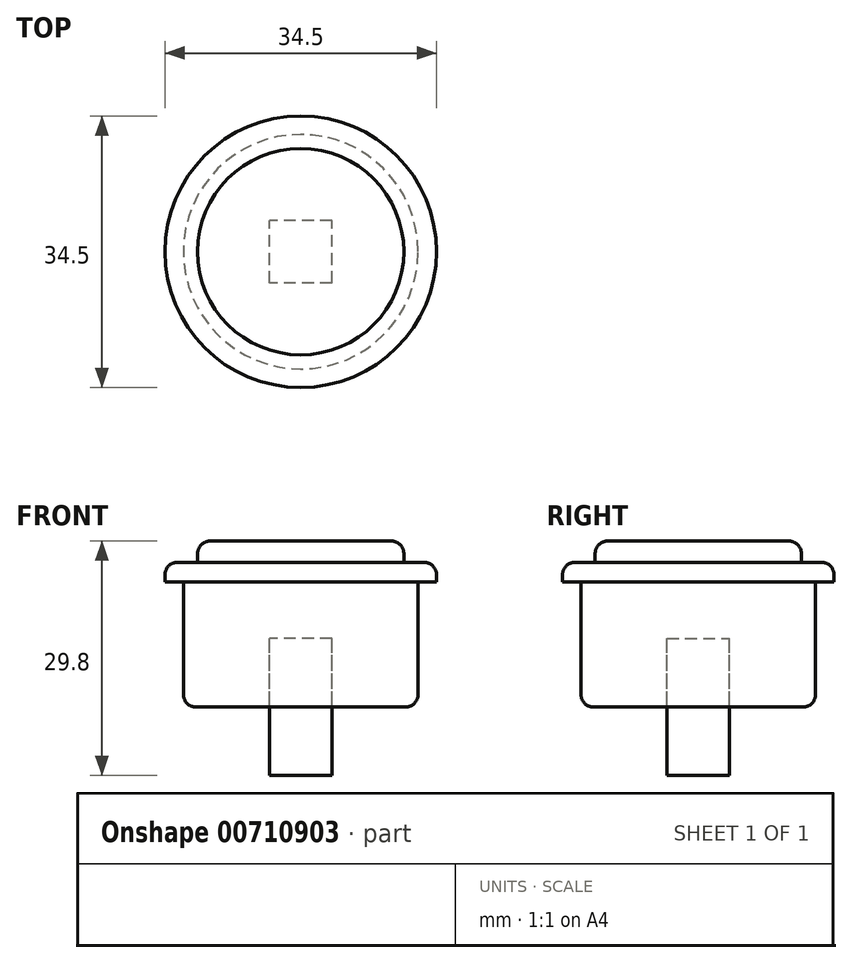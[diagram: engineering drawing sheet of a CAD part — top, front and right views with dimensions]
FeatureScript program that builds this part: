
annotation { "Feature Type Name" : "Feature", "Feature Type Description" : "" }
export const myFeature = defineFeature(function(context is Context, id is Id, definition is map)
    precondition{}
    {
        {
            var Q0;
            Q0=qCreatedBy(makeId("Top.planeOp"),FACE);
            var sketch = newSketch(context, id + "F0", { "sketchPlane" : qUnion([Q0])});
            skCircle(sketch, "E0", {"center": v(0, 0) * mm, "radius": 17.25 * mm});
            skSolve(sketch);
        }
        {
            var Q0;
            Q0 = qSketchRegion(id + "F0", true);
            extrude(context, id + "F1", {"entities" : qUnion([Q0]), "depth" : 2.5 * mm, "offsetDistance" : 25 * mm});
        }
        {
            var Q0;
            Q0=makeQuery(id+"F1.opExtrude","CAP_FACE",FACE,{"disambiguationData":[OSD([sQuery(id+"F0.wireOp",EDGE,"E0")])],"isStart":false});
            fillet(context, id + "F2", {"entities" : qUnion([Q0]), "radius" : 1.6 * mm, "tangentPropagation" : true, "allowEdgeOverflow" : false});
        }
        {
            var Q0;
            Q0=makeQuery(id+"F1.opExtrude","CAP_FACE",FACE,{"disambiguationData":[OSD([sQuery(id+"F0.wireOp",EDGE,"E0")])],"isStart":false});
            var sketch = newSketch(context, id + "F3", { "sketchPlane" : qUnion([Q0])});
            skCircle(sketch, "E1", {"center": v(0, 0) * mm, "radius": 13.1 * mm});
            skSolve(sketch);
        }
        {
            var Q0;
            Q0 = qSketchRegion(id + "F3", true);
            extrude(context, id + "F4", {"entities" : qUnion([Q0]), "operationType" : NewBodyOperationType.ADD, "depth" : 2.7 * mm, "offsetDistance" : 25 * mm});
        }
        {
            var Q0;
            Q0=makeQuery(id+"F4.opExtrude","CAP_FACE",FACE,{"disambiguationData":[OSD([sQuery(id+"F3.wireOp",EDGE,"E1")])],"isStart":false});
            fillet(context, id + "F5", {"entities" : qUnion([Q0]), "radius" : 1.6 * mm, "tangentPropagation" : true, "allowEdgeOverflow" : false});
        }
        {
            var Q0;
            Q0=makeQuery(id+"F1.opExtrude","CAP_FACE",FACE,{"disambiguationData":[OSD([sQuery(id+"F0.wireOp",EDGE,"E0")])],"isStart":true});
            var sketch = newSketch(context, id + "F6", { "sketchPlane" : qUnion([Q0])});
            skCircle(sketch, "E2", {"center": v(0, 0) * mm, "radius": 14.9 * mm});
            skSolve(sketch);
        }
        {
            var Q0;
            Q0=makeQuery(id+"F6.imprint","IMPRINT",FACE,{"disambiguationData":[TD([[makeQuery(id+"F6.imprint","IMPRINT",EDGE,{"derivedFrom":sQuery(id+"F6.wireOp",EDGE,"E2")}),1.0]])]});
            extrude(context, id + "F7", {"entities" : qUnion([Q0]), "operationType" : NewBodyOperationType.ADD, "depth" : 15.9 * mm, "offsetDistance" : 25 * mm});
        }
        {
            var Q0;
            Q0=makeQuery(id+"F7.opExtrude","CAP_FACE",FACE,{"disambiguationData":[OSD([sQuery(id+"F6.wireOp",EDGE,"E2")])],"isStart":false});
            fillet(context, id + "F8", {"entities" : qUnion([Q0]), "radius" : 1.6 * mm, "tangentPropagation" : true, "allowEdgeOverflow" : false});
        }
        {
            var Q0;
            Q0=makeQuery(id+"F7.opExtrude","CAP_FACE",FACE,{"disambiguationData":[OSD([sQuery(id+"F6.wireOp",EDGE,"E2")])],"isStart":false});
            var sketch = newSketch(context, id + "F9", { "sketchPlane" : qUnion([Q0])});
            skLineSegment(sketch, "E3.bottom", {"start": v(3.96, 3.96) * mm, "end": v(-3.96, 3.96) * mm});
            skLineSegment(sketch, "E3.top", {"start": v(3.96, -3.96) * mm, "end": v(-3.96, -3.96) * mm});
            skLineSegment(sketch, "E3.left", {"start": v(3.96, 3.96) * mm, "end": v(3.96, -3.96) * mm});
            skLineSegment(sketch, "E3.right", {"start": v(-3.96, 3.96) * mm, "end": v(-3.96, -3.96) * mm});
            skPoint(sketch, "E3.middle", {"position": v(0, 0) * mm});
            skSolve(sketch);
        }
        {
            var Q0;
            Q0 = qSketchRegion(id + "F9", true);
            extrude(context, id + "F10", {"entities" : qUnion([Q0]), "endBound" : BoundingType.SYMMETRIC, "depth" : 17.4 * mm, "offsetDistance" : 25 * mm});
        }
    });
